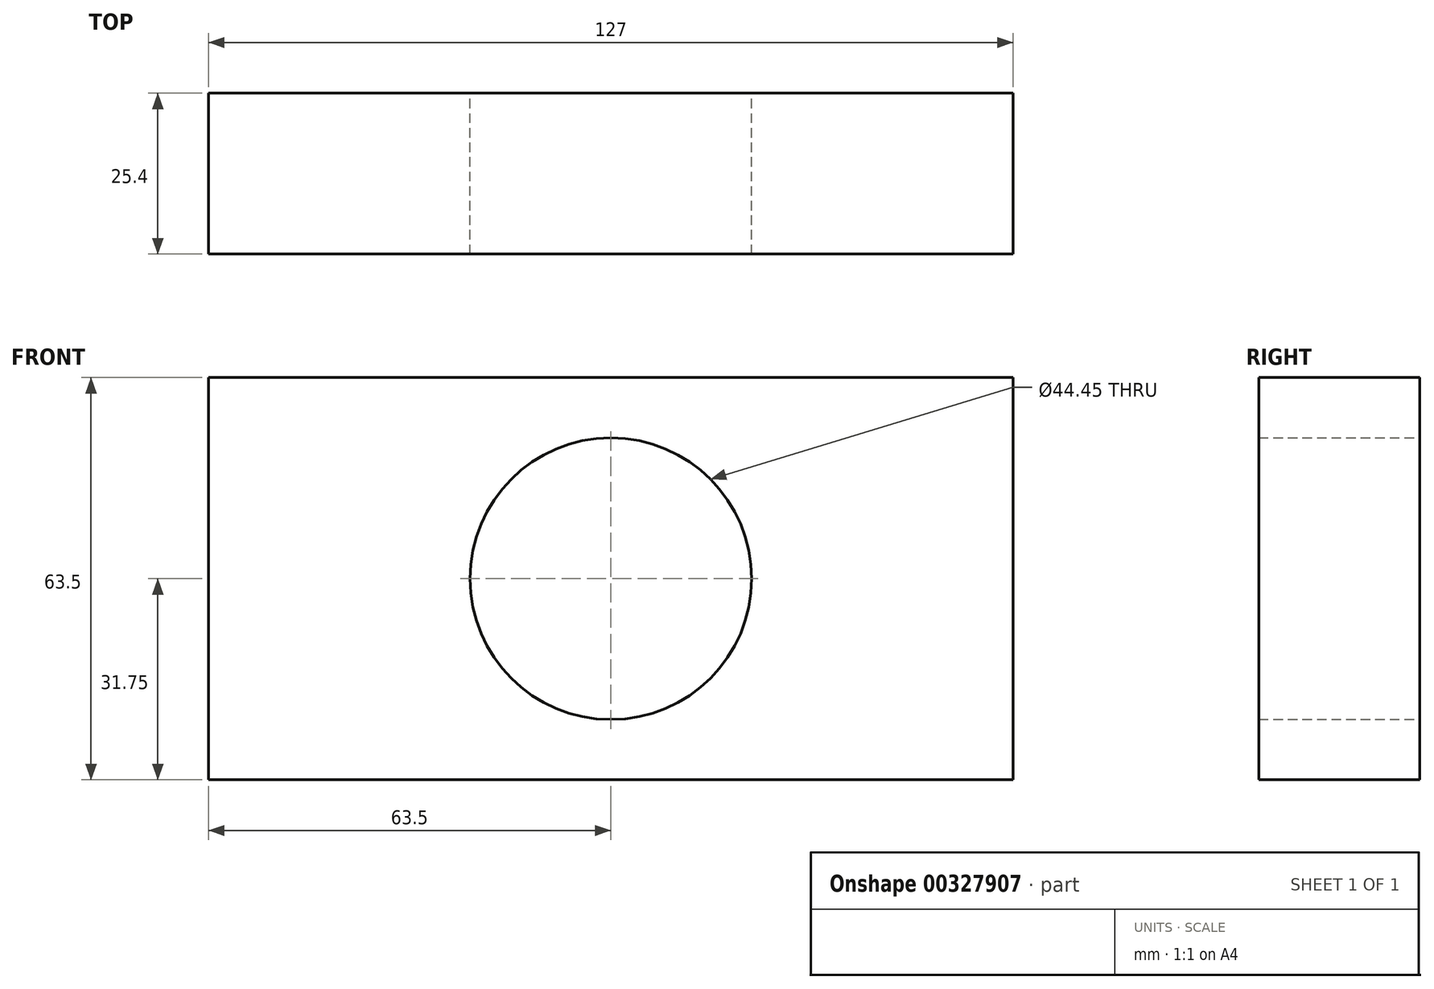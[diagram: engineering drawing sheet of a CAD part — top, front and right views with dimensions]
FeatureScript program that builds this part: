
annotation { "Feature Type Name" : "Feature", "Feature Type Description" : "" }
export const myFeature = defineFeature(function(context is Context, id is Id, definition is map)
    precondition{}
    {
        {
            var Q0;
            Q0=qCreatedBy(makeId("Front.planeOp"),FACE);
            var sketch = newSketch(context, id + "F0", { "sketchPlane" : qUnion([Q0])});
            skLineSegment(sketch, "E0.bottom", {"start": v(-63.5, -31.75) * mm, "end": v(63.5, -31.75) * mm});
            skLineSegment(sketch, "E0.top", {"start": v(-63.5, 31.75) * mm, "end": v(63.5, 31.75) * mm});
            skLineSegment(sketch, "E0.left", {"start": v(-63.5, -31.75) * mm, "end": v(-63.5, 31.75) * mm});
            skLineSegment(sketch, "E0.right", {"start": v(63.5, -31.75) * mm, "end": v(63.5, 31.75) * mm});
            skPoint(sketch, "E0.middle", {"position": v(0, 0) * mm});
            skCircle(sketch, "E1", {"center": v(0, 0) * mm, "radius": 22.23 * mm});
            skSolve(sketch);
        }
        {
            var Q0;
            Q0=makeQuery(id+"F0.imprint","IMPRINT",FACE,{"disambiguationData":[TD([[makeQuery(id+"F0.imprint","IMPRINT",EDGE,{"derivedFrom":sQuery(id+"F0.wireOp",EDGE,"E0.bottom")}),1.0]])]});
            extrude(context, id + "F1", {"entities" : qUnion([Q0]), "depth" : 25.4 * mm});
        }
    });
